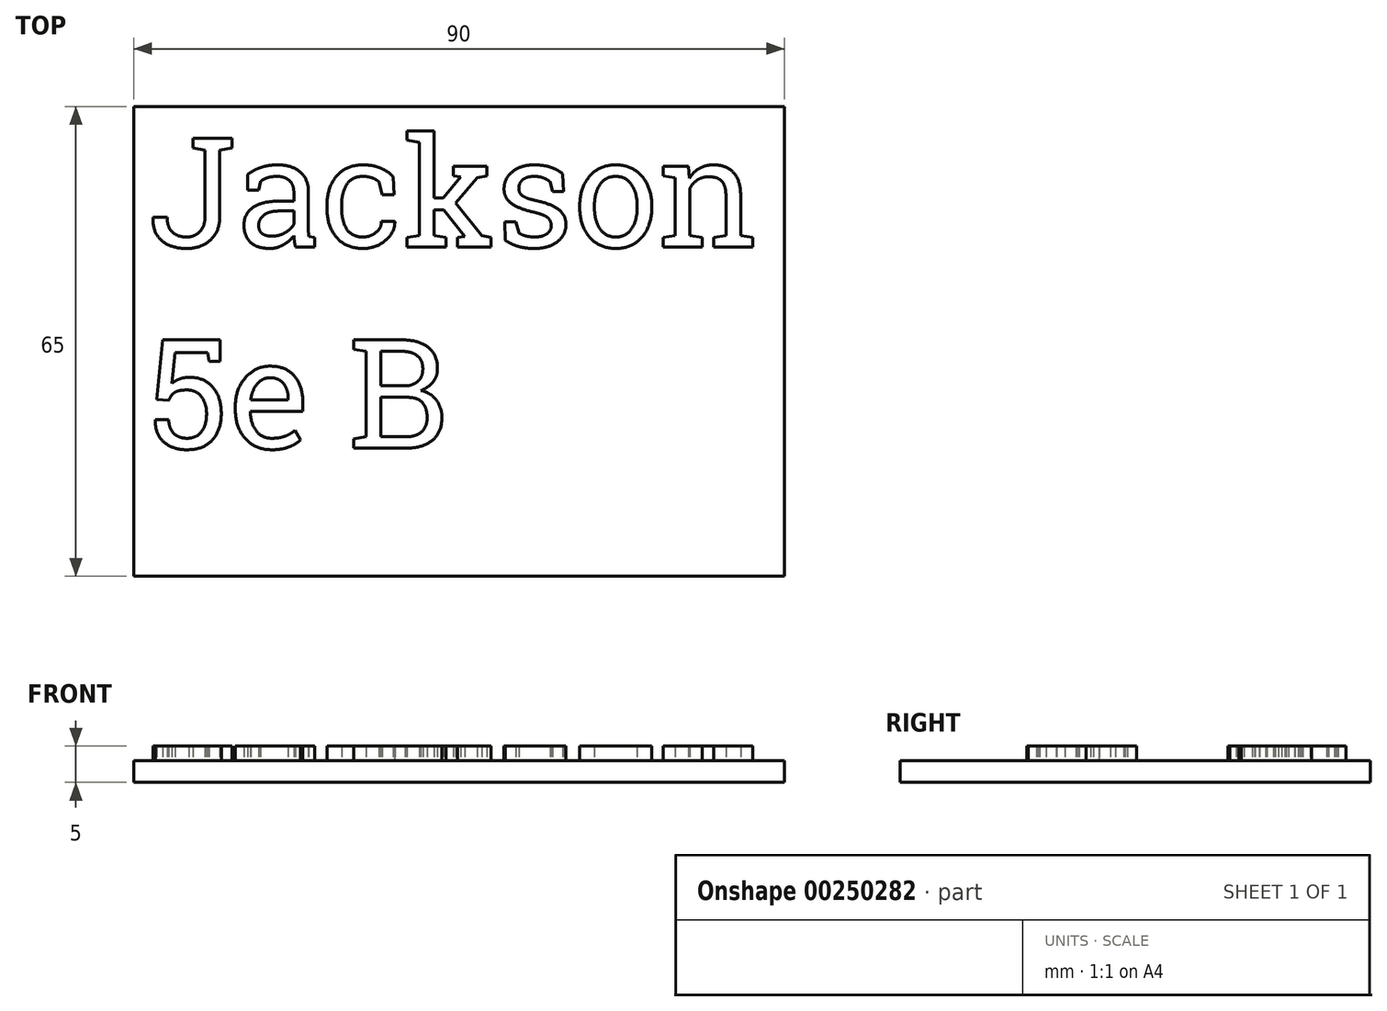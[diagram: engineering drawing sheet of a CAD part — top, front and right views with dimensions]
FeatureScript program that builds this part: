
annotation { "Feature Type Name" : "Feature", "Feature Type Description" : "" }
export const myFeature = defineFeature(function(context is Context, id is Id, definition is map)
    precondition{}
    {
        {
            var Q0;
            Q0=qCreatedBy(makeId("Top.planeOp"),FACE);
            var sketch = newSketch(context, id + "F0", { "sketchPlane" : qUnion([Q0])});
            skLineSegment(sketch, "E0.bottom", {"start": v(0, 0) * mm, "end": v(90, 0) * mm});
            skLineSegment(sketch, "E0.top", {"start": v(0, -65) * mm, "end": v(90, -65) * mm});
            skLineSegment(sketch, "E0.left", {"start": v(0, 0) * mm, "end": v(0, -65) * mm});
            skLineSegment(sketch, "E0.right", {"start": v(90, 0) * mm, "end": v(90, -65) * mm});
            skSolve(sketch);
        }
        {
            var Q0;
            Q0=makeQuery(id+"F0.imprint","IMPRINT",FACE,{"disambiguationData":[TD([[makeQuery(id+"F0.imprint","IMPRINT",EDGE,{"derivedFrom":sQuery(id+"F0.wireOp",EDGE,"E0.bottom")}),-1.0]])]});
            extrude(context, id + "F1", {"entities" : qUnion([Q0]), "depth" : 3 * mm});
        }
        {
            var Q0;
            Q0=makeQuery(id+"F1.opExtrude","CAP_FACE",FACE,{"disambiguationData":[OSD([sQuery(id+"F0.wireOp",EDGE,"E0.bottom"),sQuery(id+"F0.wireOp",EDGE,"E0.top"),sQuery(id+"F0.wireOp",EDGE,"E0.left"),sQuery(id+"F0.wireOp",EDGE,"E0.right")])],"isStart":false});
            var sketch = newSketch(context, id + "F2", { "sketchPlane" : qUnion([Q0])});
            skText(sketch, "E1", { "text": "Jackson\n5e B", "fontName": "RobotoSlab-Regular.ttf"});
            const initialGuessF2  = {"E1": [0.002, -0.01943, 1, 0, 0.01519]};
            skSetInitialGuess(sketch, initialGuessF2);
            skSolve(sketch);
        }
        {
            var Q0;
            Q0 = qSketchRegion(id + "F2", true);
            extrude(context, id + "F3", {"entities" : qUnion([Q0]), "operationType" : NewBodyOperationType.ADD, "depth" : 2 * mm});
        }
    });
